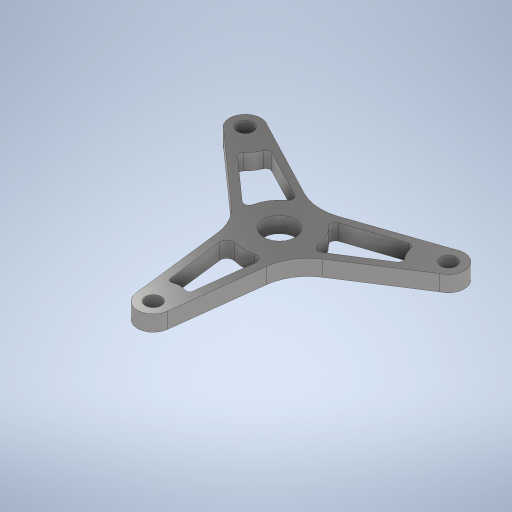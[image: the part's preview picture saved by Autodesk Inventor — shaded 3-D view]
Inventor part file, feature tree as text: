
AUTODESK INVENTOR PART (.ipt)
format: ipt  version: 2024 (Build 280153000, 153)  size: 360,960 bytes
history: native  units: mm
features: sketch x4, extrude x3, hole x2, fillet x1, pattern_circular x1
ambient origin geometry x8: Origin, YZ Plane, XZ Plane, XY Plane, X Axis, Y Axis, Z Axis, Center Point
bodies: Body1 (feature_tree)
feature tree (11):
  sketch  "Skizze1"  dims[d4=80.0mm d7=120.0deg]
  extrude  "Extrusion2"  TaperAngle=120.0deg  [1 undecoded]
  hole  "Bohrung1"  [1 undecoded]
  hole  "Bohrung2"  [1 undecoded]
  fillet  "Rundung1"  Radius=4.0mm
  extrude  "Extrusion4"  Depth=10.0mm TaperAngle=0.0deg
  pattern_circular  "Runde Anordnung1"  [2 undecoded]
  extrude  "Extrusion5"  Depth=10.0mm
  sketch  "Skizze4"  dims[d8=20.0mm d10=11.0mm]
  sketch  "Skizze5"  dims[d11=11.0mm d12=20.0mm d17=4.0mm]
  sketch  "Skizze6"  dims[d21=160.0mm d27=10.0mm d28=0.0mm d31=37.0mm d32=37.0mm d35=2.443461mm d39=2.0mm d40=35.843231mm d41=7.0mm d43=35.0mm d45=10.0mm d46=6.0mm d47=4.0mm d48=2.0mm d49=90.0deg d50=8.0mm d51=0.0mm d52=10.0mm d53=6.0mm d54=4.0mm d55=2.0mm d56=90.0deg d57=8.0mm d58=0.0mm d59=30.0mm d61=10.0mm d62=5.0mm d63=5.0mm d64=18.0mm d66=25.0mm d67=35.0mm d68=5.0mm d69=10.0mm d70=0.0mm d71=10.0mm d72=20.0mm d73=-20.943951mm d75=10.0mm d76=0.0mm d77=10.0mm]
note: 5 required parameter values undecoded (feature->parameter linkage not recoverable at this tier; creation-order binding heuristic only, values carry confidence <= 0.55)
